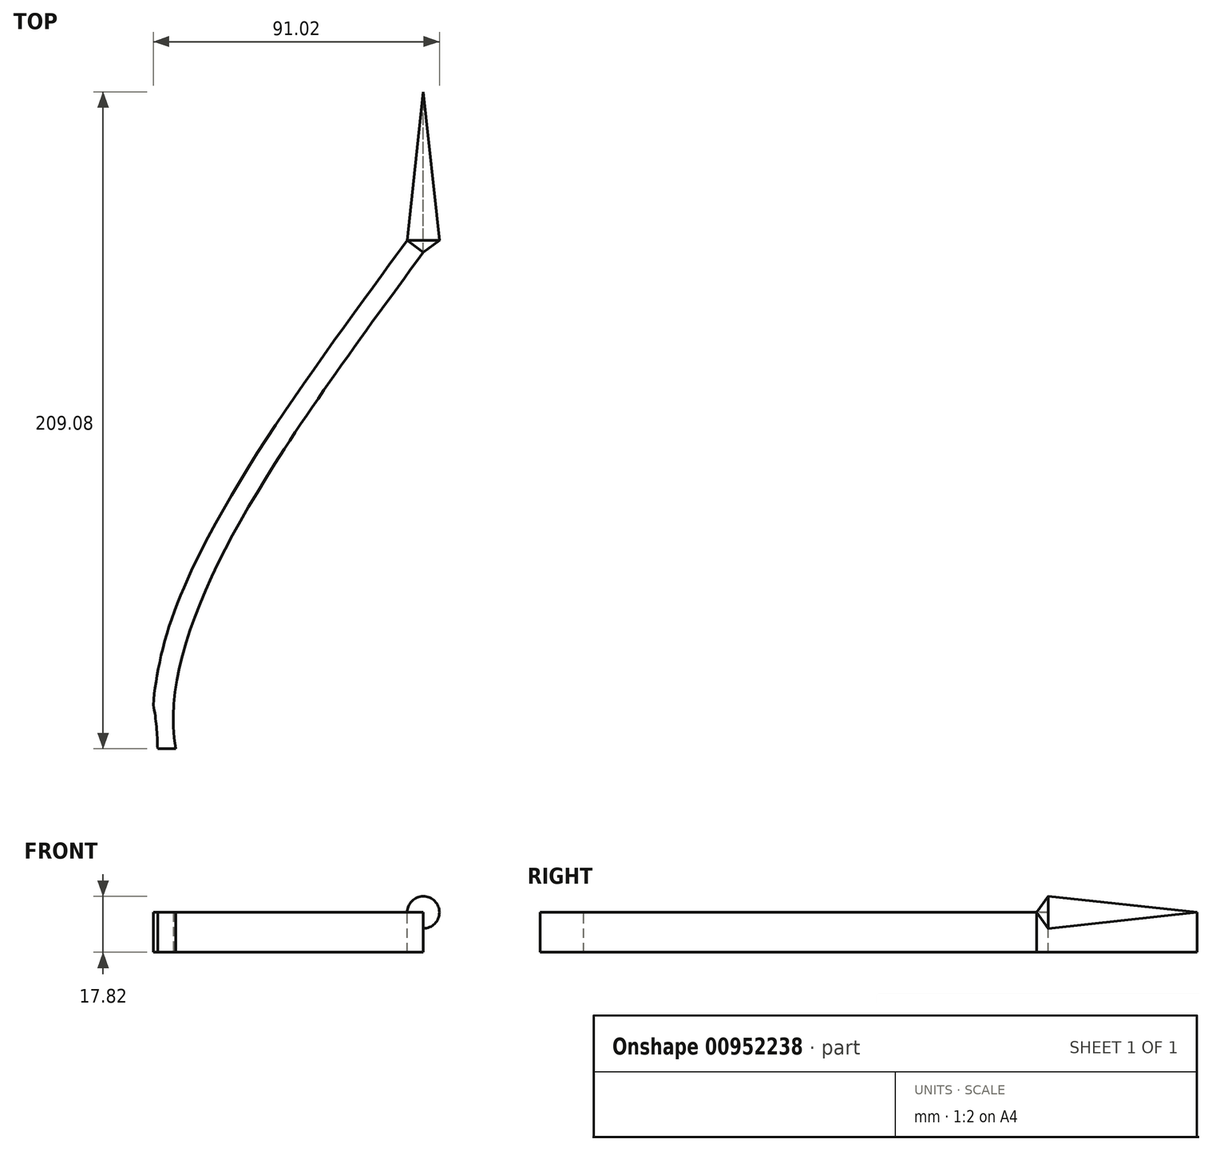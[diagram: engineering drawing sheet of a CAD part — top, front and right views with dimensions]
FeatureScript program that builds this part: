
annotation { "Feature Type Name" : "Feature", "Feature Type Description" : "" }
export const myFeature = defineFeature(function(context is Context, id is Id, definition is map)
    precondition{}
    {
        {
            var Q0;
            Q0=qCreatedBy(makeId("Top.planeOp"),FACE);
            var sketch = newSketch(context, id + "F0", { "sketchPlane" : qUnion([Q0])});
            skFitSpline(sketch, "E0", {"points": [v(0, -74.9) * mm, v(-78.75, 0) * mm, v(0, 157.99) * mm], "startDerivative": vector(-249.38, 145.84) * mm, "endDerivative": vector(230.1, 313.22) * mm});
            skLineSegment(sketch, "E1", {"start": v(0, 157.99) * mm, "end": v(0, 271.5) * mm});
            skCircle(sketch, "E2", {"center": v(-157.4, 0) * mm, "radius": 72.84 * mm});
            skArc(sketch, "E3.0", {"start": v(-219.26, -49.44) * mm, "mid": v(-169.68, -78.23) * mm, "end": v(-113.67, -66.01) * mm});
            skArc(sketch, "E4", {"start": v(-113.67, 66.01) * mm, "mid": v(-90.72, 61.38) * mm, "end": v(-68.1, 67.48) * mm});
            skArc(sketch, "E5.trimOffspring", {"start": v(-44.24, 95.37) * mm, "mid": v(-43.57, 97.41) * mm, "end": v(-42.98, 99.49) * mm});
            skLineSegment(sketch, "E6", {"start": v(-157.4, 0) * mm, "end": v(-78.22, 0) * mm});
            skArc(sketch, "E7.MirrorCS", {"start": v(-113.67, -66.01) * mm, "mid": v(-80.4, -62.77) * mm, "end": v(-52.26, -80.81) * mm});
            skArc(sketch, "E8.MirrorC", {"start": v(-334.2, -49.44) * mm, "mid": v(-475.24, 0) * mm, "end": v(-334.2, 49.44) * mm});
            skArc(sketch, "E9", {"start": v(-219.26, -49.44) * mm, "mid": v(-278.13, -23.08) * mm, "end": v(-335.99, -51.6) * mm});
            skPoint(sketch, "E9.startSnap0", {"position": v(-276.73, -49.44) * mm});
            skArc(sketch, "E10.MirrorCS", {"start": v(-219.26, 49.44) * mm, "mid": v(-278.13, 23.08) * mm, "end": v(-335.99, 51.6) * mm});
            skCircle(sketch, "E11.0", {"center": v(-396.06, 0) * mm, "radius": 72.84 * mm});
            skCircle(sketch, "E12.0", {"center": v(-396.06, 0) * mm, "radius": 66.49 * mm});
            skCircle(sketch, "E13.0", {"center": v(-157.4, 0) * mm, "radius": 66.49 * mm});
            skPoint(sketch, "E14.orphan", {"position": v(-276.73, 0) * mm});
            skFitSpline(sketch, "E15.MirrorCS", {"points": [v(0, -74.9) * mm, v(78.75, 0) * mm, v(0, 157.99) * mm], "startDerivative": vector(249.38, 145.84) * mm, "endDerivative": vector(-230.1, 313.22) * mm});
            skArc(sketch, "E16.trimOffspring", {"start": v(-113.67, 66.01) * mm, "mid": v(-169.68, 78.23) * mm, "end": v(-219.26, 49.44) * mm});
            skLineSegment(sketch, "E17.trimOffspring", {"start": v(-78.25, -2.46) * mm, "end": v(-78.25, -2.46) * mm});
            skFitSpline(sketch, "E18.0", {"points": [v(-3.2, -80.39) * mm, v(-8.4, -77.35) * mm, v(-18.84, -71.25) * mm, v(-34.09, -61.83) * mm, v(-48.43, -51.92) * mm, v(-61.33, -41.27) * mm, v(-70.45, -31.54) * mm, v(-76.45, -23.07) * mm, v(-80.21, -16.35) * mm, v(-82.64, -10.4) * mm, v(-84.1, -5.46) * mm, v(-84.95, -1.65) * mm, v(-85.53, 2.25) * mm, v(-85.96, 7.51) * mm, v(-85.88, 14.23) * mm, v(-84.88, 22.46) * mm, v(-82.45, 33.66) * mm, v(-77.54, 48.06) * mm, v(-69.18, 65.97) * mm, v(-58.78, 84.43) * mm, v(-46.76, 103.36) * mm, v(-33.53, 122.64) * mm, v(-19.51, 142.16) * mm, v(-9.91, 155.22) * mm, v(-5.12, 161.75) * mm]});
            skPoint(sketch, "E19.orphan", {"position": v(-55.57, 77.01) * mm});
            skLineSegment(sketch, "E20", {"start": v(-5.12, 161.75) * mm, "end": v(0, 209.08) * mm});
            skCircle(sketch, "E21", {"center": v(0, -185.41) * mm, "radius": 97.88 * mm});
            skCircle(sketch, "E22.0", {"center": v(0, -185.41) * mm, "radius": 104.23 * mm});
            skPoint(sketch, "E23.orphan", {"position": v(-55.57, -77.01) * mm});
            skPoint(sketch, "E24.orphan", {"position": v(0, 0) * mm});
            skLineSegment(sketch, "E25", {"start": v(0, 157.99) * mm, "end": v(-5.12, 161.75) * mm});
            skLineSegment(sketch, "E26", {"start": v(0, 0) * mm, "end": v(0, 60.79) * mm});
            skArc(sketch, "E27.MirrorCS", {"start": v(113.67, 66.01) * mm, "mid": v(90.72, 61.38) * mm, "end": v(68.1, 67.48) * mm});
            skArc(sketch, "E28.MirrorCS", {"start": v(113.67, -66.01) * mm, "mid": v(80.4, -62.77) * mm, "end": v(52.26, -80.81) * mm});
            skArc(sketch, "E29.MirrorCS", {"start": v(52.26, -80.81) * mm, "mid": v(0, -302.34) * mm, "end": v(-52.26, -80.81) * mm});
            skPoint(sketch, "E30.orphan", {"position": v(10.18, -68.93) * mm});
            skPoint(sketch, "E31.orphan", {"position": v(-10.18, -68.93) * mm});
            skCircle(sketch, "E32.MirrorC", {"center": v(157.4, 0) * mm, "radius": 72.84 * mm});
            skArc(sketch, "E33.MirrorCS", {"start": v(219.26, -49.44) * mm, "mid": v(169.68, -78.23) * mm, "end": v(113.67, -66.01) * mm});
            skArc(sketch, "E34.MirrorCS", {"start": v(219.26, -49.44) * mm, "mid": v(278.13, -23.08) * mm, "end": v(335.99, -51.6) * mm});
            skArc(sketch, "E35.MirrorCS", {"start": v(219.26, 49.44) * mm, "mid": v(278.13, 23.08) * mm, "end": v(335.99, 51.6) * mm});
            skArc(sketch, "E36.MirrorCS", {"start": v(113.67, 66.01) * mm, "mid": v(169.68, 78.23) * mm, "end": v(219.26, 49.44) * mm});
            skCircle(sketch, "E37.MirrorC", {"center": v(157.4, 0) * mm, "radius": 66.49 * mm});
            skCircle(sketch, "E38.MirrorC", {"center": v(396.06, 0) * mm, "radius": 72.84 * mm});
            skCircle(sketch, "E39.MirrorC", {"center": v(396.06, 0) * mm, "radius": 66.49 * mm});
            skArc(sketch, "E40.MirrorCS", {"start": v(334.2, -49.44) * mm, "mid": v(475.24, 0) * mm, "end": v(334.2, 49.44) * mm});
            skFitSpline(sketch, "E41.0", {"points": [v(84.44, -3.87) * mm, v(84.78, -2.42) * mm, v(85.32, 0.52) * mm, v(85.8, 5.01) * mm, v(85.95, 9.57) * mm, v(85.73, 15.74) * mm, v(84.71, 23.6) * mm, v(81.68, 36.45) * mm, v(75.52, 53.05) * mm, v(65.06, 73.76) * mm, v(52.17, 95.15) * mm, v(37.47, 117.08) * mm, v(21.58, 139.35) * mm, v(10.6, 154.29) * mm, v(5.12, 161.75) * mm]});
            skLineSegment(sketch, "E42", {"start": v(5.12, 161.75) * mm, "end": v(0, 209.08) * mm});
            skSolve(sketch);
        }
        {
            var Q0;
            {var subQ2=sQuery(id+"F0.wireOp",EDGE,"E20");Q0=makeQuery(id+"F0.imprint","IMPRINT",FACE,{"disambiguationData":[TD([[makeQuery(id+"F0.imprint","IMPRINT",EDGE,{"derivedFrom":subQ2}),-1.0]])]});}
            var Q1;
            Q1=sQuery(id+"F0.wireOp",EDGE,"E1");
            revolve(context, id + "F1", {"surfaceOperationType" : NewSurfaceOperationType.NEW, "entities" : qUnion([Q0]), "axis" : qUnion([Q1]), "revolveType" : RevolveType.FULL});
        }
        {
            var Q0;
            {var subQ15=sQuery(id+"F0.wireOp",EDGE,"E0");Q0=makeQuery(id+"F0.imprint","IMPRINT",FACE,{"disambiguationData":[TD([[makeQuery(id+"F0.imprint","IMPRINT",EDGE,{"derivedFrom":subQ15}),1.0]])]});}
            var Q1;
            {var subQ2=sQuery(id+"F0.wireOp",EDGE,"E20");Q1=makeQuery(id+"F0.imprint","IMPRINT",FACE,{"disambiguationData":[TD([[makeQuery(id+"F0.imprint","IMPRINT",EDGE,{"derivedFrom":subQ2}),-1.0]])]});}
            extrude(context, id + "F2", {"entities" : qUnion([Q0, Q1]), "operationType" : NewBodyOperationType.ADD, "oppositeDirection" : true, "depth" : 12.7 * mm, "offsetDistance" : 25.4 * mm});
        }
        {
            var Q0;
            {var subQ4=sQuery(id+"F0.wireOp",EDGE,"E0");Q0=makeQuery(id+"F0.imprint","IMPRINT",FACE,{"disambiguationData":[TD([[makeQuery(id+"F0.imprint","IMPRINT",EDGE,{"derivedFrom":subQ4}),-1.0]])]});}
            var Q1;
            Q1=sQuery(id+"F0.wireOp",EDGE,"E0");
            var Q2;
            Q2=sQuery(id+"F0.wireOp",EDGE,"E26");
            revolve(context, id + "F3", {"bodyType" : ToolBodyType.SURFACE, "surfaceOperationType" : NewSurfaceOperationType.NEW, "entities" : qUnion([Q0]), "surfaceEntities" : qUnion([Q1]), "axis" : qUnion([Q2]), "revolveType" : RevolveType.ONE_DIRECTION, "oppositeDirection" : true, "angle" : 180 * degree});
        }
        {
            var Q0;
            Q0=sQuery(id+"F0.wireOp",EDGE,"E0");
            var Q1;
            Q1=sQuery(id+"F0.wireOp",EDGE,"E26");
            revolve(context, id + "F4", {"bodyType" : ToolBodyType.SURFACE, "surfaceOperationType" : NewSurfaceOperationType.NEW, "surfaceEntities" : qUnion([Q0]), "axis" : qUnion([Q1]), "revolveType" : RevolveType.FULL});
        }
    });
